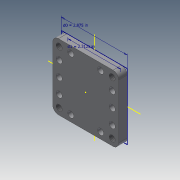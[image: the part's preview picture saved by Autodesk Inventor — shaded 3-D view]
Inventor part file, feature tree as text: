
AUTODESK INVENTOR PART (.ipt)
format: ipt  version: 2020.3 (Build 243373000, 373)  size: 172,544 bytes
history: native  units: in
note: dims shown in document units (in); Inventor stores cm internally (conversion verified against a paired STEP export)
features: sketch x3, hole x2, extrude x1, fillet x1
ambient origin geometry x8: Origin, YZ Plane, XZ Plane, XY Plane, X Axis, Y Axis, Z Axis, Center Point
bodies: Solid1 (feature_tree)
feature tree (7):
  sketch  "Sketch1"  dims[d0=2.875in d1=2.3125in]
  extrude  "Extrusion1"  Depth=2.875in
  hole  "Hole1"  [1 undecoded]
  hole  "Hole2"  [1 undecoded]
  fillet  "Fillet1"  Radius=0.7874in
  sketch  "Sketch3"  dims[d4=0.2617in d5=0.63in d6=0.375in d7=0.25in d8=0.5635in d9=0.874in d10=0.8108in d12=0.7874in d13=0.26in d14=0.63in d15=0.496in d16=0.25in d17=90.0deg d18=0.874in d19=0.8108in d20=0.25in d21=0.7874in]
  sketch  "Sketch2"  dims[d2=0.375in d3=0.0in]
note: 2 required parameter values undecoded (feature->parameter linkage not recoverable at this tier; creation-order binding heuristic only, values carry confidence <= 0.55)
